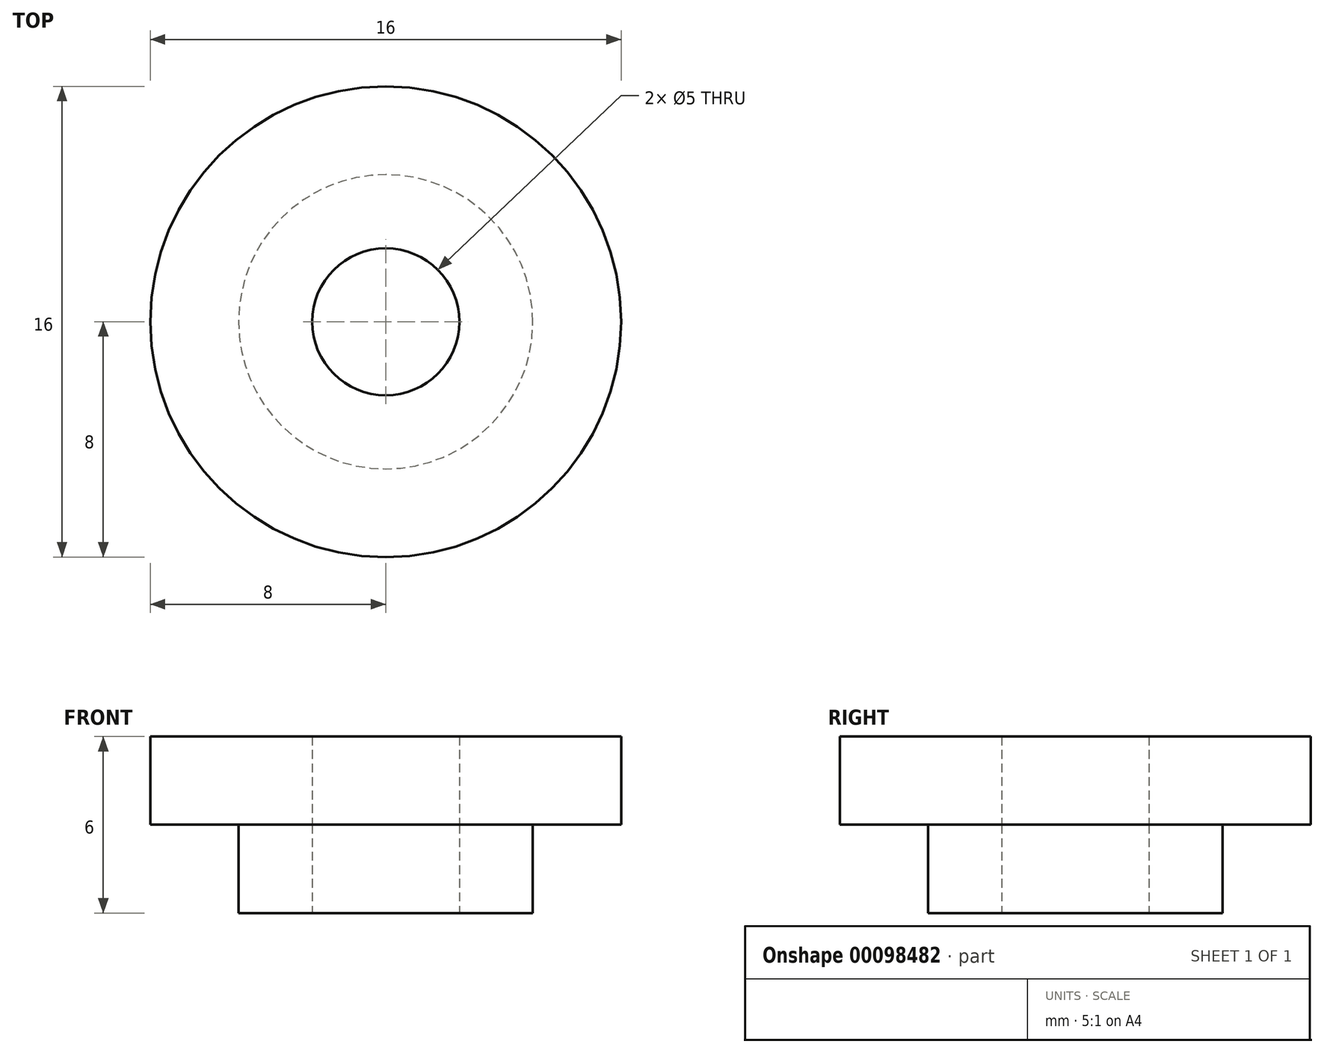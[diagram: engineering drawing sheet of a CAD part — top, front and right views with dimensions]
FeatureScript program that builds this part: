
annotation { "Feature Type Name" : "Feature", "Feature Type Description" : "" }
export const myFeature = defineFeature(function(context is Context, id is Id, definition is map)
    precondition{}
    {
        {
            var Q0;
            Q0=qCreatedBy(makeId("Top.planeOp"),FACE);
            var sketch = newSketch(context, id + "F0", { "sketchPlane" : qUnion([Q0])});
            skCircle(sketch, "E0", {"center": v(0, 0) * mm, "radius": 5 * mm});
            skCircle(sketch, "E1", {"center": v(0, 0) * mm, "radius": 2.5 * mm});
            skSolve(sketch);
        }
        {
            var Q0;
            Q0 = qSketchRegion(id + "F0", true);
            extrude(context, id + "F1", {"entities" : qUnion([Q0]), "depth" : 3 * mm, "offsetDistance" : 25 * mm});
        }
        {
            var Q0;
            Q0=makeQuery(id+"F1.opExtrude","CAP_FACE",FACE,{"disambiguationData":[OSD([sQuery(id+"F0.wireOp",EDGE,"E0"),sQuery(id+"F0.wireOp",EDGE,"E1")])],"isStart":false});
            var sketch = newSketch(context, id + "F2", { "sketchPlane" : qUnion([Q0])});
            skCircle(sketch, "E2.0", {"center": v(0, 0) * mm, "radius": 2.5 * mm});
            skCircle(sketch, "E3", {"center": v(0, 0) * mm, "radius": 8 * mm});
            skSolve(sketch);
        }
        {
            var Q0;
            Q0 = qSketchRegion(id + "F2", true);
            extrude(context, id + "F3", {"entities" : qUnion([Q0]), "depth" : 3 * mm, "offsetDistance" : 25 * mm});
        }
    });
